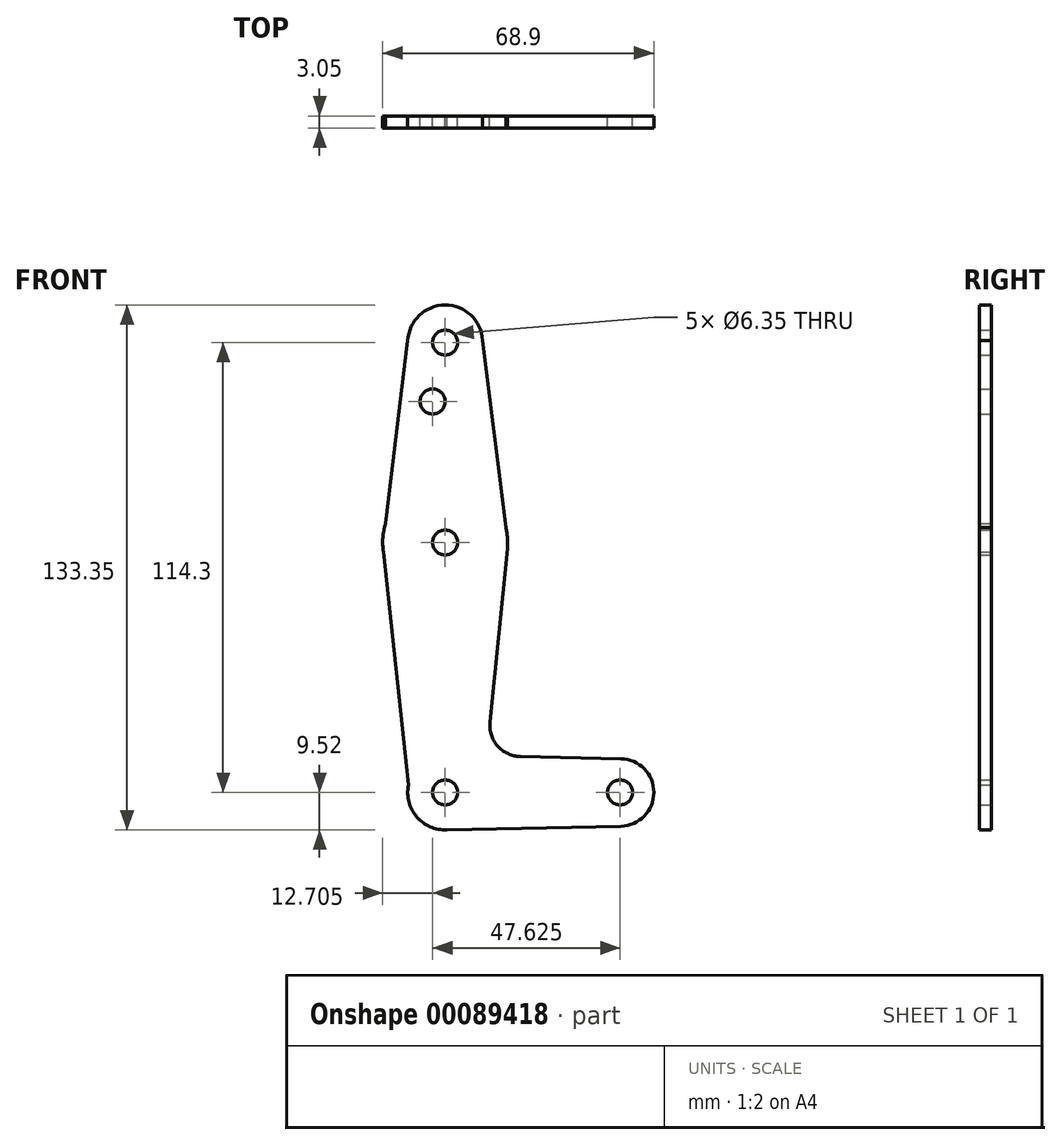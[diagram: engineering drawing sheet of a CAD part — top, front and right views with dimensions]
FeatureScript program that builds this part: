
annotation { "Feature Type Name" : "Feature", "Feature Type Description" : "" }
export const myFeature = defineFeature(function(context is Context, id is Id, definition is map)
    precondition{}
    {
        {
            var Q0;
            Q0=qCreatedBy(makeId("Front.planeOp"),FACE);
            var sketch = newSketch(context, id + "F0", { "sketchPlane" : qUnion([Q0])});
            skLineSegment(sketch, "E0", {"start": v(0, 114.3) * mm, "end": v(0, 0) * mm, "construction": true});
            skLineSegment(sketch, "E1", {"start": v(0, 0) * mm, "end": v(44.45, 0) * mm});
            skCircle(sketch, "E2", {"center": v(0, 114.3) * mm, "radius": 9.53 * mm});
            skCircle(sketch, "E3", {"center": v(0, 63.5) * mm, "radius": 15.88 * mm});
            skCircle(sketch, "E4", {"center": v(0, 0) * mm, "radius": 9.53 * mm});
            skCircle(sketch, "E5", {"center": v(44.45, 0) * mm, "radius": 8.57 * mm});
            skLineSegment(sketch, "E6", {"start": v(15.8, 61.91) * mm, "end": v(11.37, 17.86) * mm});
            skLineSegment(sketch, "E7", {"start": v(19.1, 9.12) * mm, "end": v(44.63, 8.57) * mm});
            skLineSegment(sketch, "E8", {"start": v(0, -9.53) * mm, "end": v(44.63, -8.57) * mm});
            skCircle(sketch, "E9", {"center": v(0, 114.3) * mm, "radius": 3.18 * mm});
            skCircle(sketch, "E10", {"center": v(-3.18, 99.32) * mm, "radius": 3.18 * mm});
            skCircle(sketch, "E11", {"center": v(0, 63.5) * mm, "radius": 3.18 * mm});
            skCircle(sketch, "E12", {"center": v(0, 0) * mm, "radius": 3.18 * mm});
            skCircle(sketch, "E13", {"center": v(44.45, 0) * mm, "radius": 3.18 * mm});
            skArc(sketch, "E14.filletArc", {"start": v(11.37, 17.86) * mm, "mid": v(13.33, 11.8) * mm, "end": v(19.1, 9.12) * mm});
            skLineSegment(sketch, "E15", {"start": v(-9.35, 116.1) * mm, "end": v(-15.13, 68.32) * mm});
            skLineSegment(sketch, "E16", {"start": v(-15.69, 61.08) * mm, "end": v(-8.74, -3.78) * mm});
            skLineSegment(sketch, "E17", {"start": v(9.5, 114.85) * mm, "end": v(15.4, 67.36) * mm});
            skSolve(sketch);
        }
        {
            var Q0;
            Q0 = qSketchRegion(id + "F0", true);
            extrude(context, id + "F1", {"entities" : qUnion([Q0]), "depth" : 3.05 * mm});
        }
    });
